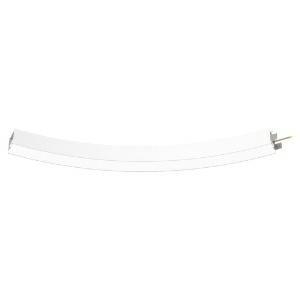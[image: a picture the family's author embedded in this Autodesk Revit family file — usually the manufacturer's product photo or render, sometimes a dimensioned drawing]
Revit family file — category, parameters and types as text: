
# Revit family: super-g_slim_super_g_slim_3000_45deg_hl_ps_led__24w_3160lm_3000k_cri_80_430-1700_61c5
name_source: partatom
category: Leuchten
revit_build: Autodesk Revit 2016 (Build: 20190508_0715(x64)
units: mm (PartAtom-declared; Revit-internal decimal feet)

## family parameters
Basisbauteil = Fläche
Beim Laden mit Abzugskörper schneiden = Nein
Bemaßung runder Anschluss = Durchmesser verwenden
Gemeinsam genutzt = Nein
Lichtquelle = Nein
Raumberechnungspunkt = Nein
Teiletyp = Normal

## types (1)
- 430-1700-D01 (1 x LED, 480 lm, 3000K)
    Approval mark = CE
    Beschreibung = The insert consists of aluminum-extruded profile. Charming SOFT-EDGE design ensure unparalleled styling. The ballast is integrated and allows for an operation with 220-240V (50/60Hz). SUPER-G SLIM (# 430-1700) ist not dimmable (on/off).
    CIE Flux Codes = 48 79 96 100 71
    Color Rendering = 1B/80…89
    Color Temperature = 3000K
    Height = 90 mm
    Hersteller = Prolicht
    Lamp Light Flux = 480 lm
    Lamp count = 1
    Lampe = 1 x LED
    Length = 144 mm
    Luminous efficacy = 103 lm/W
    ModVariant = Nein
    Modell = 430-1700
    Mounting Place = Ceiling
    Mounting Type = Pendant
    Number of Poles = 1
    OnlyDefault = Ja
    Power Factor = 1
    Product Name = SUPER-G SLIM__SUPER G SLIM 3000/45° HL PS LED: 24W 3160lm 3000K CRI:80
    Product group = Suspended profile systems
    ProductGroupID = 944
    Protection Class = Protection class I
    Protection Degree = IP 20
    RLX_Detail_Level = 1
    RlxData = <blob elided: 29933 chars, md5=ea522f7d>
    Scheinlast = 26 VA
    Socket = socket
    Standby Power = 0 W
    System Light Flux = 2723 lm
    System Power = 26 W
    Typenbild = 430-1700.jpg
    URL = http://relux.com
    VarID = 430-1700-d01
    Voltage = 0 V
    Vorgabe-Ansicht = 1800 mm
    Weight = 0.00 kg
    Width = 65 mm

## geometry (parser evidence)
native form markers: Blend x4, Sweep x30
no freeform markers — native parametric forms only
